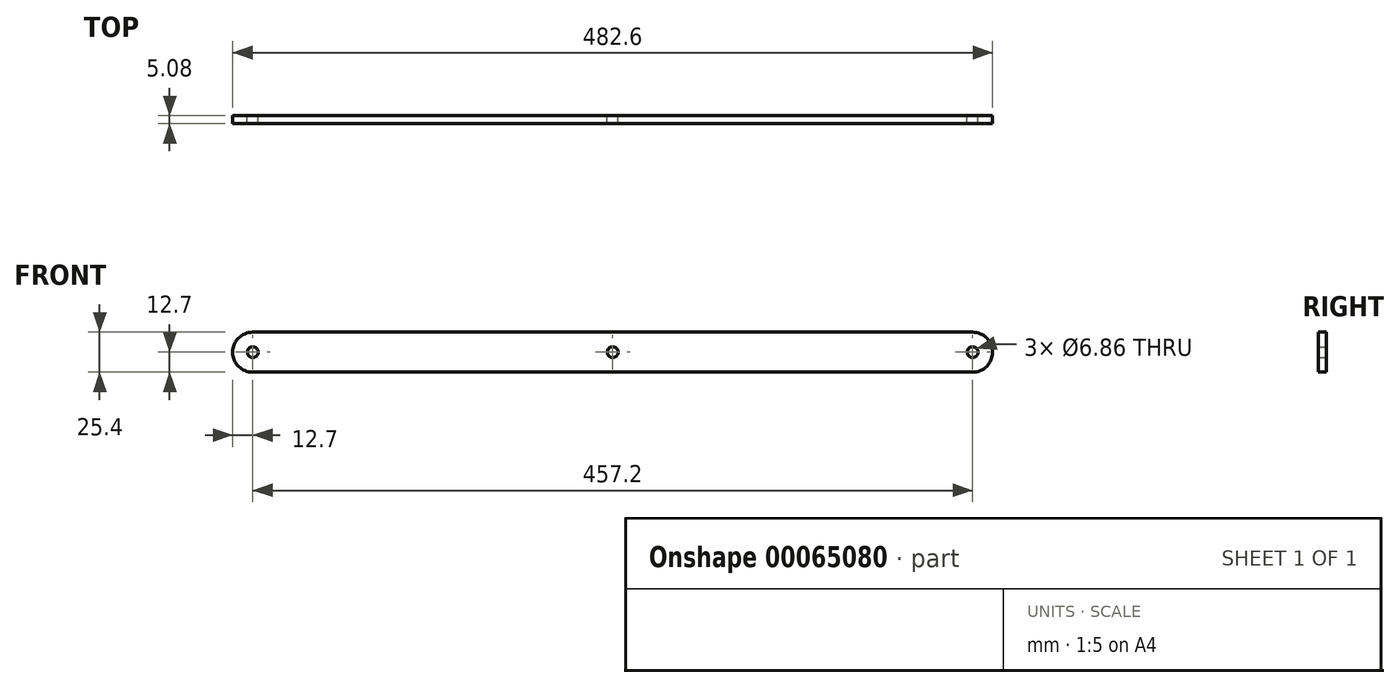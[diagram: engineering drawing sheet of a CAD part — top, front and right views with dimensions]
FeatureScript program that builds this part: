
annotation { "Feature Type Name" : "Feature", "Feature Type Description" : "" }
export const myFeature = defineFeature(function(context is Context, id is Id, definition is map)
    precondition{}
    {
        {
            var Q0;
            Q0=qCreatedBy(makeId("Front.planeOp"),FACE);
            var sketch = newSketch(context, id + "F0", { "sketchPlane" : qUnion([Q0])});
            skLineSegment(sketch, "E0", {"start": v(-293.24, 0) * mm, "end": v(311.28, 0) * mm, "construction": true});
            skLineSegment(sketch, "E1", {"start": v(0, 12.7) * mm, "end": v(-228.6, 12.7) * mm});
            skLineSegment(sketch, "E2", {"start": v(0, 12.7) * mm, "end": v(228.6, 12.7) * mm});
            skLineSegment(sketch, "E3", {"start": v(0, -12.7) * mm, "end": v(-228.6, -12.7) * mm});
            skLineSegment(sketch, "E4", {"start": v(0, -12.7) * mm, "end": v(228.6, -12.7) * mm});
            skArc(sketch, "E5", {"start": v(228.6, 12.7) * mm, "mid": v(241.3, 0) * mm, "end": v(228.6, -12.7) * mm});
            skArc(sketch, "E6", {"start": v(-228.6, 12.7) * mm, "mid": v(-241.3, 0) * mm, "end": v(-228.6, -12.7) * mm});
            skCircle(sketch, "E7", {"center": v(-228.6, 0) * mm, "radius": 3.43 * mm});
            skCircle(sketch, "E8", {"center": v(0, 0) * mm, "radius": 3.43 * mm});
            skCircle(sketch, "E9", {"center": v(228.6, 0) * mm, "radius": 3.43 * mm});
            skSolve(sketch);
        }
        {
            var Q0;
            Q0=makeQuery(id+"F0.imprint","IMPRINT",FACE,{"disambiguationData":[TD([[makeQuery(id+"F0.imprint","IMPRINT",EDGE,{"derivedFrom":sQuery(id+"F0.wireOp",EDGE,"E1")}),1.0]])]});
            extrude(context, id + "F1", {"entities" : qUnion([Q0]), "flatOperationType" : FlatOperationType.REMOVE, "offsetDistance" : 25.4 * mm, "depth" : 5.08 * mm, "domain" : OperationDomain.MODEL});
        }
    });
